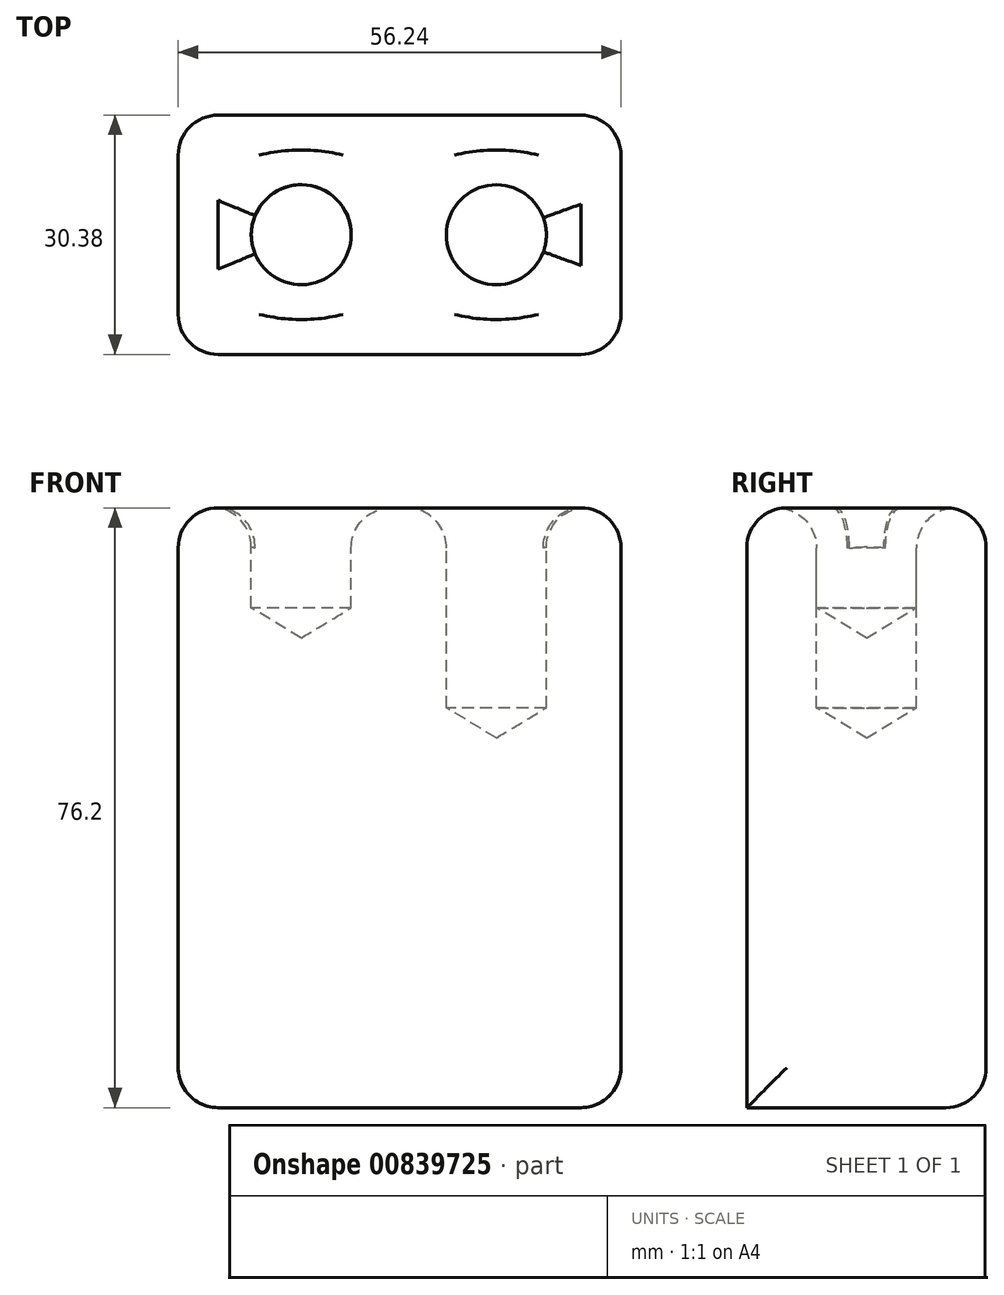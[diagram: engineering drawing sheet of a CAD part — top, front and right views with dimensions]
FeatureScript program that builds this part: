
annotation { "Feature Type Name" : "Feature", "Feature Type Description" : "" }
export const myFeature = defineFeature(function(context is Context, id is Id, definition is map)
    precondition{}
    {
        {
            var Q0;
            Q0=qCreatedBy(makeId("Top.planeOp"),FACE);
            var sketch = newSketch(context, id + "F0", { "sketchPlane" : qUnion([Q0])});
            skLineSegment(sketch, "E0.bottom", {"start": v(28.12, -15.19) * mm, "end": v(-28.12, -15.19) * mm});
            skLineSegment(sketch, "E0.top", {"start": v(28.12, 15.19) * mm, "end": v(-28.12, 15.19) * mm});
            skLineSegment(sketch, "E0.left", {"start": v(28.12, -15.19) * mm, "end": v(28.12, 15.19) * mm});
            skLineSegment(sketch, "E0.right", {"start": v(-28.12, -15.19) * mm, "end": v(-28.12, 15.19) * mm});
            skPoint(sketch, "E0.middle", {"position": v(0, 0) * mm});
            skSolve(sketch);
        }
        {
            var Q0;
            Q0=makeQuery(id+"F0.imprint","IMPRINT",FACE,{"disambiguationData":[TD([[makeQuery(id+"F0.imprint","IMPRINT",EDGE,{"derivedFrom":sQuery(id+"F0.wireOp",EDGE,"E0.bottom")}),-1.0]])]});
            extrude(context, id + "F1", {"entities" : qUnion([Q0]), "depth" : 76.2 * mm, "offsetDistance" : 25.4 * mm});
        }
        {
            var Q0;
            Q0=makeQuery(id+"F1.opExtrude","CAP_FACE",FACE,{"disambiguationData":[OSD([sQuery(id+"F0.wireOp",EDGE,"E0.bottom"),sQuery(id+"F0.wireOp",EDGE,"E0.top"),sQuery(id+"F0.wireOp",EDGE,"E0.left"),sQuery(id+"F0.wireOp",EDGE,"E0.right")])],"isStart":false});
            var sketch = newSketch(context, id + "F2", { "sketchPlane" : qUnion([Q0])});
            skCircle(sketch, "E1", {"center": v(-12.48, 0) * mm, "radius": 5.19 * mm});
            skCircle(sketch, "E2", {"center": v(13.08, 0) * mm, "radius": 6.23 * mm});
            skSolve(sketch);
        }
        {
            var Q0;
            Q0=sQuery(id+"F2.wireOp",VERTEX,"E1.center");
            var Q1;
            Q1=makeQuery(id+"F1.opExtrude","SWEPT_BODY",BODY,{"disambiguationData":[OSD([sQuery(id+"F0.wireOp",EDGE,"E0.bottom"),sQuery(id+"F0.wireOp",EDGE,"E0.top"),sQuery(id+"F0.wireOp",EDGE,"E0.left"),sQuery(id+"F0.wireOp",EDGE,"E0.right")])]});
            hole(context, id + "F3", {"style" : HoleStyle.SIMPLE, "endStyle" : HoleEndStyle.BLIND, "holeDiameter" : 12.7 * mm, "majorDiameter" : 6.35 * mm, "holeDepth" : 12.7 * mm, "isTappedThrough" : true, "tappedDepth" : 12.7 * mm, "tapClearance" : 3, "locations" : qUnion([Q0]), "scope" : qUnion([Q1])});
        }
        {
            var Q0;
            Q0=makeQuery(id+"F1.opExtrude","CAP_FACE",FACE,{"disambiguationData":[OSD([sQuery(id+"F0.wireOp",EDGE,"E0.bottom"),sQuery(id+"F0.wireOp",EDGE,"E0.top"),sQuery(id+"F0.wireOp",EDGE,"E0.left"),sQuery(id+"F0.wireOp",EDGE,"E0.right")])],"isStart":false});
            var sketch = newSketch(context, id + "F4", { "sketchPlane" : qUnion([Q0])});
            skCircle(sketch, "E3", {"center": v(12.3, 0) * mm, "radius": 6.33 * mm});
            skSolve(sketch);
        }
        {
            var Q0;
            Q0=makeQuery(id+"F1.opExtrude","SWEPT_FACE",FACE,{"disambiguationData":[OSD([sQuery(id+"F0.wireOp",EDGE,"E0.right")])]});
            fillet(context, id + "F5", {"entities" : qUnion([Q0]), "radius" : 5.08 * mm, "tangentPropagation" : true, "allowEdgeOverflow" : false});
        }
        {
            var Q0;
            Q0=makeQuery(id+"F1.opExtrude","SWEPT_FACE",FACE,{"disambiguationData":[OSD([sQuery(id+"F0.wireOp",EDGE,"E0.left")])]});
            fillet(context, id + "F6", {"entities" : qUnion([Q0]), "radius" : 5.08 * mm, "tangentPropagation" : true, "allowEdgeOverflow" : false});
        }
        {
            var Q0;
            Q0=sQuery(id+"F4.wireOp",VERTEX,"E3.center");
            var Q1;
            Q1=makeQuery(id+"F1.opExtrude","SWEPT_BODY",BODY,{"disambiguationData":[OSD([sQuery(id+"F0.wireOp",EDGE,"E0.bottom"),sQuery(id+"F0.wireOp",EDGE,"E0.top"),sQuery(id+"F0.wireOp",EDGE,"E0.left"),sQuery(id+"F0.wireOp",EDGE,"E0.right")])]});
            hole(context, id + "F7", {"style" : HoleStyle.SIMPLE, "endStyle" : HoleEndStyle.BLIND, "holeDiameter" : 12.7 * mm, "majorDiameter" : 6.35 * mm, "holeDepth" : 25.4 * mm, "isTappedThrough" : true, "tappedDepth" : 12.7 * mm, "tapClearance" : 3, "locations" : qUnion([Q0]), "scope" : qUnion([Q1])});
        }
        {
            var Q0;
            Q0=makeQuery(id+"F1.opExtrude","SWEPT_FACE",FACE,{"disambiguationData":[OSD([sQuery(id+"F0.wireOp",EDGE,"E0.top")])]});
            var Q1;
            Q1=makeQuery(id+"F1.opExtrude","CAP_FACE",FACE,{"disambiguationData":[OSD([sQuery(id+"F0.wireOp",EDGE,"E0.bottom"),sQuery(id+"F0.wireOp",EDGE,"E0.top"),sQuery(id+"F0.wireOp",EDGE,"E0.left"),sQuery(id+"F0.wireOp",EDGE,"E0.right")])],"isStart":false});
            fillet(context, id + "F8", {"entities" : qUnion([Q0, Q1]), "radius" : 5.08 * mm, "tangentPropagation" : true, "allowEdgeOverflow" : false});
        }
    });
